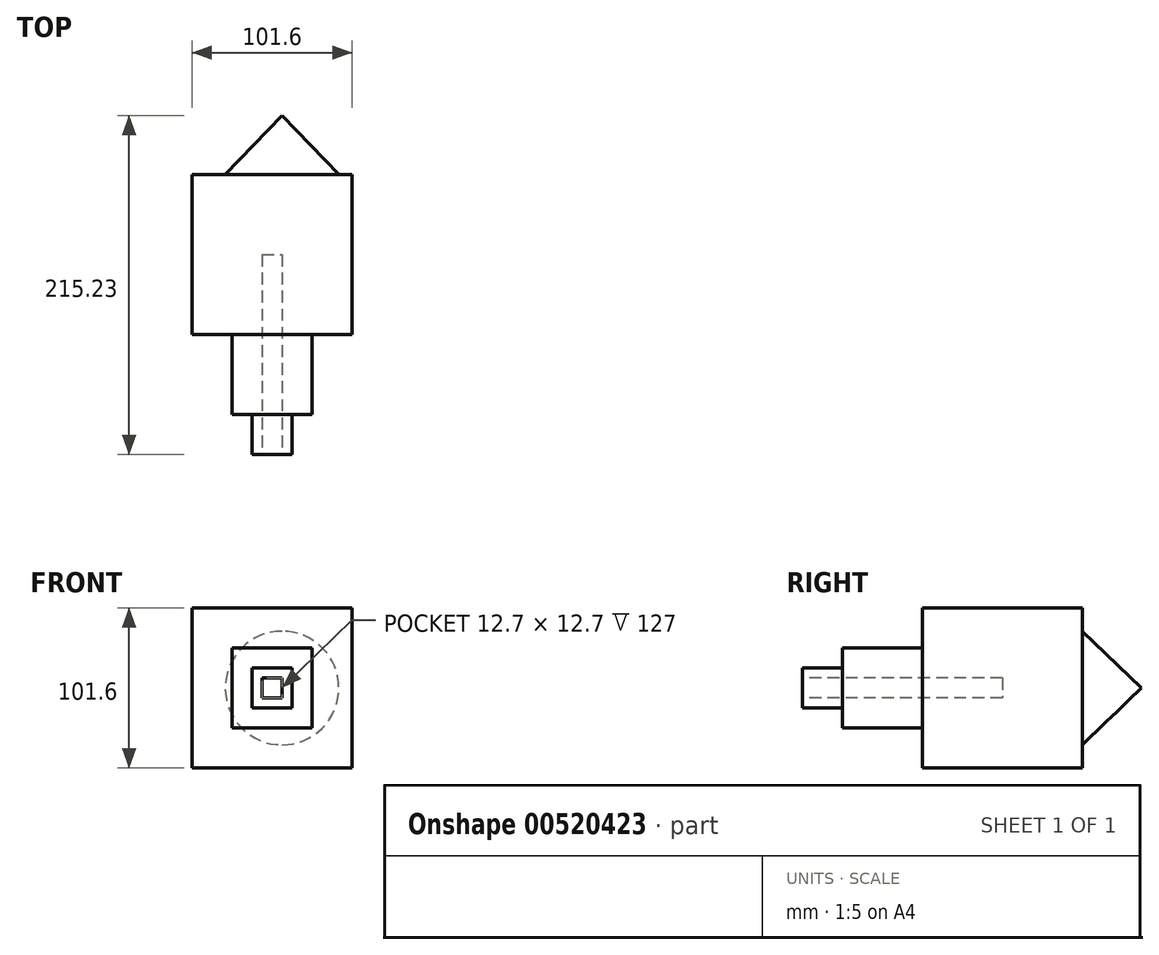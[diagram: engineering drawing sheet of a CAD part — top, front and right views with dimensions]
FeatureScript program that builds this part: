
annotation { "Feature Type Name" : "Feature", "Feature Type Description" : "" }
export const myFeature = defineFeature(function(context is Context, id is Id, definition is map)
    precondition{}
    {
        {
            var Q0;
            Q0=qCreatedBy(makeId("Front.planeOp"),FACE);
            var sketch = newSketch(context, id + "F0", { "sketchPlane" : qUnion([Q0])});
            skLineSegment(sketch, "E0.bottom", {"start": v(38.96, 61.52) * mm, "end": v(-62.64, 61.52) * mm});
            skLineSegment(sketch, "E0.top", {"start": v(38.96, -40.08) * mm, "end": v(-62.64, -40.08) * mm});
            skLineSegment(sketch, "E0.left", {"start": v(38.96, 61.52) * mm, "end": v(38.96, -40.08) * mm});
            skLineSegment(sketch, "E0.right", {"start": v(-62.64, 61.52) * mm, "end": v(-62.64, -40.08) * mm});
            skPoint(sketch, "E0.middle", {"position": v(-11.84, 10.72) * mm});
            skSolve(sketch);
        }
        {
            var Q0;
            Q0=makeQuery(id+"F0.imprint","IMPRINT",FACE,{"disambiguationData":[TD([[makeQuery(id+"F0.imprint","IMPRINT",EDGE,{"derivedFrom":sQuery(id+"F0.wireOp",EDGE,"E0.bottom")}),1.0]])]});
            extrude(context, id + "F1", {"entities" : qUnion([Q0]), "depth" : 101.6 * mm, "offsetDistance" : 25.4 * mm});
        }
        {
            var Q0;
            Q0=makeQuery(id+"F1.opExtrude","CAP_FACE",FACE,{"disambiguationData":[OSD([sQuery(id+"F0.wireOp",EDGE,"E0.bottom"),sQuery(id+"F0.wireOp",EDGE,"E0.top"),sQuery(id+"F0.wireOp",EDGE,"E0.left"),sQuery(id+"F0.wireOp",EDGE,"E0.right")])],"isStart":false});
            var sketch = newSketch(context, id + "F2", { "sketchPlane" : qUnion([Q0])});
            skLineSegment(sketch, "E1.bottom", {"start": v(13.56, 36.12) * mm, "end": v(-37.24, 36.12) * mm});
            skLineSegment(sketch, "E1.top", {"start": v(13.56, -14.68) * mm, "end": v(-37.24, -14.68) * mm});
            skLineSegment(sketch, "E1.left", {"start": v(13.56, 36.12) * mm, "end": v(13.56, -14.68) * mm});
            skLineSegment(sketch, "E1.right", {"start": v(-37.24, 36.12) * mm, "end": v(-37.24, -14.68) * mm});
            skPoint(sketch, "E1.middle", {"position": v(-11.84, 10.72) * mm});
            skSolve(sketch);
        }
        {
            var Q0;
            Q0=makeQuery(id+"F2.imprint","IMPRINT",FACE,{"disambiguationData":[TD([[makeQuery(id+"F2.imprint","IMPRINT",EDGE,{"derivedFrom":sQuery(id+"F2.wireOp",EDGE,"E1.bottom")}),1.0]])]});
            extrude(context, id + "F3", {"entities" : qUnion([Q0]), "operationType" : NewBodyOperationType.ADD, "depth" : 50.8 * mm, "offsetDistance" : 25.4 * mm});
        }
        {
            var Q0;
            Q0=makeQuery(id+"F3.opExtrude","CAP_FACE",FACE,{"disambiguationData":[OSD([sQuery(id+"F2.wireOp",EDGE,"E1.bottom"),sQuery(id+"F2.wireOp",EDGE,"E1.top"),sQuery(id+"F2.wireOp",EDGE,"E1.left"),sQuery(id+"F2.wireOp",EDGE,"E1.right")])],"isStart":false});
            var sketch = newSketch(context, id + "F4", { "sketchPlane" : qUnion([Q0])});
            skLineSegment(sketch, "E2.bottom", {"start": v(-24.54, 23.42) * mm, "end": v(0.86, 23.42) * mm});
            skLineSegment(sketch, "E2.top", {"start": v(-24.54, -1.98) * mm, "end": v(0.86, -1.98) * mm});
            skLineSegment(sketch, "E2.left", {"start": v(-24.54, 23.42) * mm, "end": v(-24.54, -1.98) * mm});
            skLineSegment(sketch, "E2.right", {"start": v(0.86, 23.42) * mm, "end": v(0.86, -1.98) * mm});
            skSolve(sketch);
        }
        {
            var Q0;
            Q0=makeQuery(id+"F4.imprint","IMPRINT",FACE,{"disambiguationData":[TD([[makeQuery(id+"F4.imprint","IMPRINT",EDGE,{"derivedFrom":sQuery(id+"F4.wireOp",EDGE,"E2.bottom")}),-1.0]])]});
            extrude(context, id + "F5", {"entities" : qUnion([Q0]), "operationType" : NewBodyOperationType.ADD, "depth" : 25.4 * mm, "offsetDistance" : 25.4 * mm});
        }
        {
            var Q0;
            Q0=makeQuery(id+"F5.opExtrude","CAP_FACE",FACE,{"disambiguationData":[OSD([sQuery(id+"F4.wireOp",EDGE,"E2.bottom"),sQuery(id+"F4.wireOp",EDGE,"E2.top"),sQuery(id+"F4.wireOp",EDGE,"E2.left"),sQuery(id+"F4.wireOp",EDGE,"E2.right")])],"isStart":false});
            var sketch = newSketch(context, id + "F6", { "sketchPlane" : qUnion([Q0])});
            skLineSegment(sketch, "E3.bottom", {"start": v(-18.19, 17.07) * mm, "end": v(-5.49, 17.07) * mm});
            skLineSegment(sketch, "E3.top", {"start": v(-18.19, 4.37) * mm, "end": v(-5.49, 4.37) * mm});
            skLineSegment(sketch, "E3.left", {"start": v(-18.19, 17.07) * mm, "end": v(-18.19, 4.37) * mm});
            skLineSegment(sketch, "E3.right", {"start": v(-5.49, 17.07) * mm, "end": v(-5.49, 4.37) * mm});
            skSolve(sketch);
        }
        {
            var Q0;
            Q0=makeQuery(id+"F6.imprint","IMPRINT",FACE,{"disambiguationData":[TD([[makeQuery(id+"F6.imprint","IMPRINT",EDGE,{"derivedFrom":sQuery(id+"F6.wireOp",EDGE,"E3.bottom")}),-1.0]])]});
            extrude(context, id + "F7", {"entities" : qUnion([Q0]), "operationType" : NewBodyOperationType.REMOVE, "oppositeDirection" : true, "depth" : 127 * mm, "offsetDistance" : 25.4 * mm});
        }
        {
            var Q0;
            Q0=qCreatedBy(makeId("Top.planeOp"),FACE);
            var sketch = newSketch(context, id + "F8", { "sketchPlane" : qUnion([Q0])});
            skLineSegment(sketch, "E4", {"start": v(-22.06, 37.43) * mm, "end": v(-22.06, 0) * mm});
            skLineSegment(sketch, "E5", {"start": v(-22.06, 0) * mm, "end": v(14.04, 0) * mm});
            skLineSegment(sketch, "E6", {"start": v(14.04, 0) * mm, "end": v(-22.06, 37.43) * mm});
            skSolve(sketch);
        }
        {
            var Q0;
            Q0=makeQuery(id+"F8.imprint","IMPRINT",FACE,{"disambiguationData":[TD([[makeQuery(id+"F8.imprint","IMPRINT",EDGE,{"derivedFrom":sQuery(id+"F8.wireOp",EDGE,"E4")}),1.0]])]});
            var Q1;
            Q1=sQuery(id+"F8.wireOp",EDGE,"E4");
            revolve(context, id + "F9", {"entities" : qUnion([Q0]), "axis" : qUnion([Q1]), "revolveType" : RevolveType.FULL});
        }
        {
            var Q0;
            Q0=makeQuery(id+"F9.opRevolve","SWEPT_BODY",BODY,{"disambiguationData":[OSD([sQuery(id+"F8.wireOp",EDGE,"E4"),sQuery(id+"F8.wireOp",EDGE,"E5"),sQuery(id+"F8.wireOp",EDGE,"E6")])]});
            transform(context, id + "F10", {"entities" : qUnion([Q0]), "transformType" : TransformType.TRANSLATION_3D, "dx" : 16.5 * mm, "dy" : 0 * mm, "dz" : 10.67 * mm, "makeCopy" : false});
        }
    });
